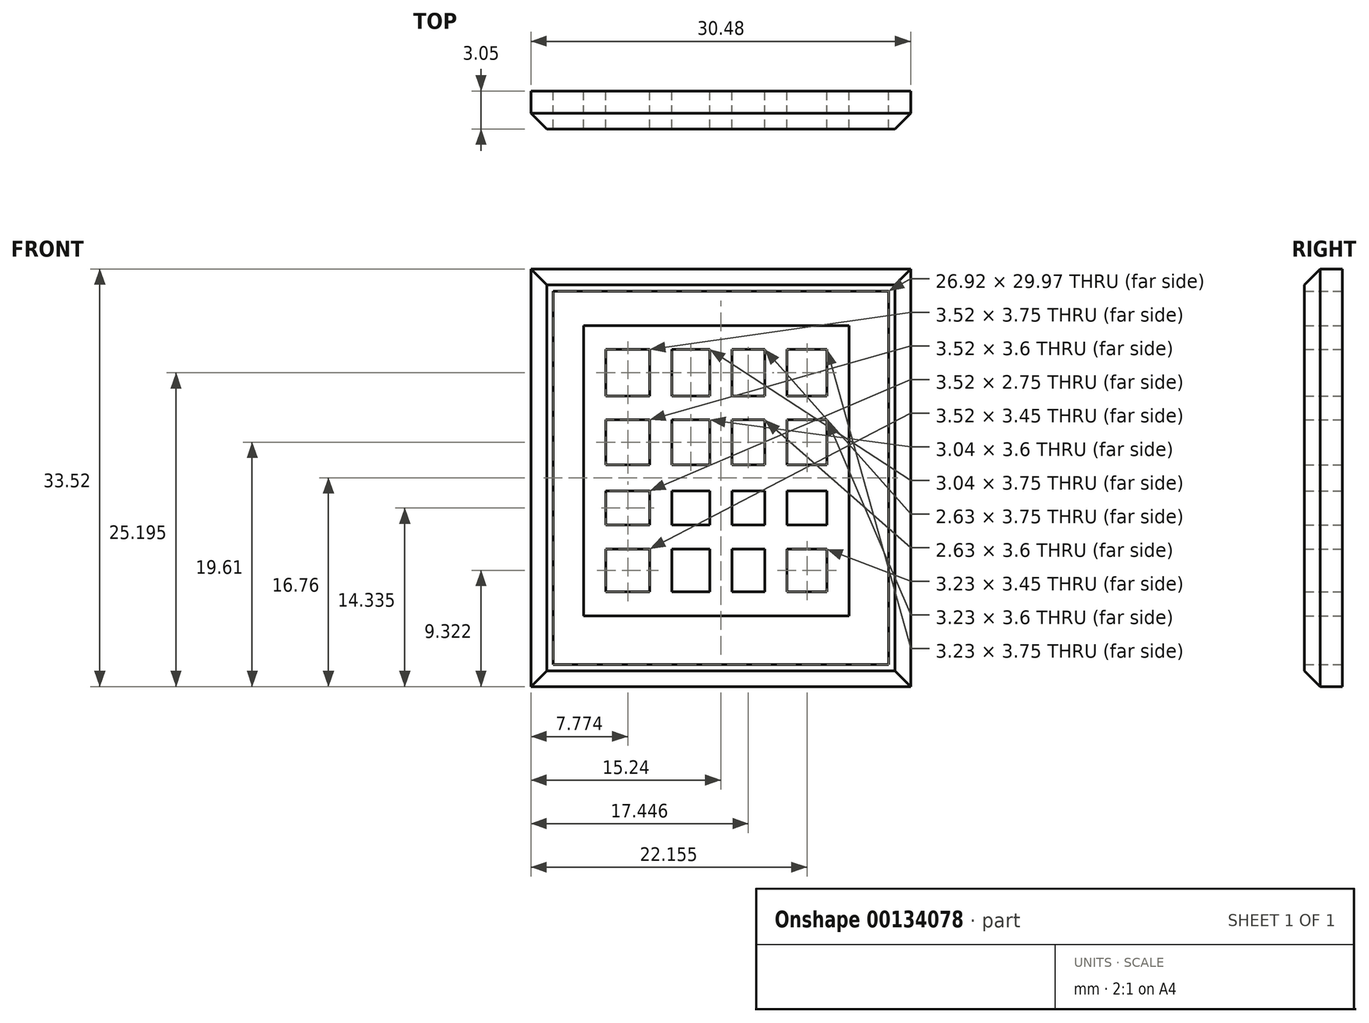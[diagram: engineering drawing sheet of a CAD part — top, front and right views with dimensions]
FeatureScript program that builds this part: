
annotation { "Feature Type Name" : "Feature", "Feature Type Description" : "" }
export const myFeature = defineFeature(function(context is Context, id is Id, definition is map)
    precondition{}
    {
        {
            var Q0;
            Q0=qCreatedBy(makeId("Front.planeOp"),FACE);
            var sketch = newSketch(context, id + "F0", { "sketchPlane" : qUnion([Q0])});
            skLineSegment(sketch, "E0.bottom", {"start": v(-15.24, 16.76) * mm, "end": v(15.24, 16.76) * mm});
            skLineSegment(sketch, "E0.top", {"start": v(-15.24, -16.76) * mm, "end": v(15.24, -16.76) * mm});
            skLineSegment(sketch, "E0.left", {"start": v(-15.24, 16.76) * mm, "end": v(-15.24, -16.76) * mm});
            skLineSegment(sketch, "E0.right", {"start": v(15.24, 16.76) * mm, "end": v(15.24, -16.76) * mm});
            skPoint(sketch, "E0.middle", {"position": v(0, 0) * mm});
            skLineSegment(sketch, "E1.bottom", {"start": v(-13.46, 14.99) * mm, "end": v(13.46, 14.99) * mm});
            skLineSegment(sketch, "E1.top", {"start": v(-13.46, -14.99) * mm, "end": v(13.46, -14.99) * mm});
            skLineSegment(sketch, "E1.left", {"start": v(-13.46, 14.99) * mm, "end": v(-13.46, -14.99) * mm});
            skLineSegment(sketch, "E1.right", {"start": v(13.46, 14.99) * mm, "end": v(13.46, -14.99) * mm});
            skLineSegment(sketch, "E2.bottom", {"start": v(-0.89, 14.99) * mm, "end": v(0.89, 14.99) * mm});
            skLineSegment(sketch, "E2.top", {"start": v(-0.89, -14.99) * mm, "end": v(0.89, -14.99) * mm});
            skLineSegment(sketch, "E2.left", {"start": v(-0.89, 14.99) * mm, "end": v(-0.89, -14.99) * mm});
            skLineSegment(sketch, "E2.right", {"start": v(0.89, 14.99) * mm, "end": v(0.89, -14.99) * mm});
            skLineSegment(sketch, "E3.bottom", {"start": v(3.52, 14.99) * mm, "end": v(5.3, 14.99) * mm});
            skLineSegment(sketch, "E3.top", {"start": v(3.52, -14.99) * mm, "end": v(5.3, -14.99) * mm});
            skLineSegment(sketch, "E3.left", {"start": v(3.52, 14.99) * mm, "end": v(3.52, -14.99) * mm});
            skLineSegment(sketch, "E3.right", {"start": v(5.3, 14.99) * mm, "end": v(5.3, -14.99) * mm});
            skPoint(sketch, "E3.middle", {"position": v(4.41, 0) * mm});
            skLineSegment(sketch, "E4.bottom", {"start": v(8.53, 14.99) * mm, "end": v(10.3, 14.99) * mm});
            skLineSegment(sketch, "E4.top", {"start": v(8.53, -14.99) * mm, "end": v(10.3, -14.99) * mm});
            skLineSegment(sketch, "E4.left", {"start": v(8.53, 14.99) * mm, "end": v(8.53, -14.99) * mm});
            skLineSegment(sketch, "E4.right", {"start": v(10.3, 14.99) * mm, "end": v(10.3, -14.99) * mm});
            skPoint(sketch, "E4.middle", {"position": v(9.42, 0) * mm});
            skLineSegment(sketch, "E5.bottom", {"start": v(-5.7, 14.99) * mm, "end": v(-3.93, 14.99) * mm});
            skLineSegment(sketch, "E5.top", {"start": v(-5.7, -14.99) * mm, "end": v(-3.93, -14.99) * mm});
            skLineSegment(sketch, "E5.left", {"start": v(-5.7, 14.99) * mm, "end": v(-5.7, -14.99) * mm});
            skLineSegment(sketch, "E5.right", {"start": v(-3.93, 14.99) * mm, "end": v(-3.93, -14.99) * mm});
            skPoint(sketch, "E5.middle", {"position": v(-4.82, 0) * mm});
            skLineSegment(sketch, "E6.bottom", {"start": v(-11, 14.99) * mm, "end": v(-9.23, 14.99) * mm});
            skLineSegment(sketch, "E6.top", {"start": v(-11, -14.99) * mm, "end": v(-9.23, -14.99) * mm});
            skLineSegment(sketch, "E6.left", {"start": v(-11, 14.99) * mm, "end": v(-11, -14.99) * mm});
            skLineSegment(sketch, "E6.right", {"start": v(-9.23, 14.99) * mm, "end": v(-9.23, -14.99) * mm});
            skPoint(sketch, "E6.middle", {"position": v(-10.12, 0) * mm});
            skLineSegment(sketch, "E7.bottom", {"start": v(-13.46, 1.05) * mm, "end": v(13.46, 1.05) * mm});
            skLineSegment(sketch, "E7.top", {"start": v(-13.46, -1.05) * mm, "end": v(13.46, -1.05) * mm});
            skLineSegment(sketch, "E7.left", {"start": v(-13.46, 1.05) * mm, "end": v(-13.46, -1.05) * mm});
            skLineSegment(sketch, "E7.right", {"start": v(13.46, 1.05) * mm, "end": v(13.46, -1.05) * mm});
            skLineSegment(sketch, "E8.bottom", {"start": v(-13.46, 6.56) * mm, "end": v(13.46, 6.56) * mm});
            skLineSegment(sketch, "E8.top", {"start": v(-13.46, 4.65) * mm, "end": v(13.46, 4.65) * mm});
            skLineSegment(sketch, "E8.left", {"start": v(-13.46, 6.56) * mm, "end": v(-13.46, 4.65) * mm});
            skLineSegment(sketch, "E8.right", {"start": v(13.46, 6.56) * mm, "end": v(13.46, 4.65) * mm});
            skPoint(sketch, "E8.middle", {"position": v(0, 5.6) * mm});
            skLineSegment(sketch, "E9.bottom", {"start": v(-13.46, 10.3) * mm, "end": v(13.46, 10.3) * mm});
            skLineSegment(sketch, "E9.top", {"start": v(-13.46, 12.22) * mm, "end": v(13.46, 12.22) * mm});
            skLineSegment(sketch, "E9.left", {"start": v(-13.46, 10.3) * mm, "end": v(-13.46, 12.22) * mm});
            skLineSegment(sketch, "E9.right", {"start": v(13.46, 10.3) * mm, "end": v(13.46, 12.22) * mm});
            skPoint(sketch, "E9.middle", {"position": v(0, 11.26) * mm});
            skLineSegment(sketch, "E10.bottom", {"start": v(-13.46, -5.71) * mm, "end": v(13.46, -5.71) * mm});
            skLineSegment(sketch, "E10.top", {"start": v(-13.46, -3.8) * mm, "end": v(13.46, -3.8) * mm});
            skLineSegment(sketch, "E10.left", {"start": v(-13.46, -5.71) * mm, "end": v(-13.46, -3.8) * mm});
            skLineSegment(sketch, "E10.right", {"start": v(13.46, -5.71) * mm, "end": v(13.46, -3.8) * mm});
            skPoint(sketch, "E10.middle", {"position": v(0, -4.76) * mm});
            skLineSegment(sketch, "E11.bottom", {"start": v(-13.46, -11.08) * mm, "end": v(13.46, -11.08) * mm});
            skLineSegment(sketch, "E11.top", {"start": v(-13.46, -9.16) * mm, "end": v(13.46, -9.16) * mm});
            skLineSegment(sketch, "E11.left", {"start": v(-13.46, -11.08) * mm, "end": v(-13.46, -9.16) * mm});
            skLineSegment(sketch, "E11.right", {"start": v(13.46, -11.08) * mm, "end": v(13.46, -9.16) * mm});
            skPoint(sketch, "E11.middle", {"position": v(0, -10.12) * mm});
            skSolve(sketch);
        }
        {
            var Q0;
            Q0=makeQuery(id+"F0.imprint","IMPRINT",FACE,{"disambiguationData":[TD([[makeQuery(id+"F0.imprint","IMPRINT",EDGE,{"derivedFrom":sQuery(id+"F0.wireOp",EDGE,"E0.bottom")}),-1.0]])]});
            var Q1;
            {var subQ0=sQuery(id+"F0.wireOp",EDGE,"E6.bottom");Q1=makeQuery(id+"F0.imprint","IMPRINT",FACE,{"disambiguationData":[TD([[makeQuery(id+"F0.imprint","IMPRINT",EDGE,{"derivedFrom":subQ0}),-1.0]])]});}
            var Q2;
            {var subQ0=sQuery(id+"F0.wireOp",EDGE,"E9.top");var subQ1=sQuery(id+"F0.wireOp",EDGE,"E6.left");var subQ2=makeQuery(id+"F0.imprint","INTERSECT",VERTEX,{"derivedFrom":[subQ1,subQ0]});Q2=makeQuery(id+"F0.imprint","IMPRINT",FACE,{"disambiguationData":[TD([[makeQuery(id+"F0.imprint","IMPRINT",EDGE,{"disambiguationData":[TD([[subQ2,-1.0]])],"derivedFrom":subQ1}),1.0]])]});}
            var Q3;
            {var subQ0=sQuery(id+"F0.wireOp",EDGE,"E9.bottom");var subQ1=sQuery(id+"F0.wireOp",EDGE,"E6.left");var subQ2=makeQuery(id+"F0.imprint","INTERSECT",VERTEX,{"derivedFrom":[subQ1,subQ0]});Q3=makeQuery(id+"F0.imprint","IMPRINT",FACE,{"disambiguationData":[TD([[makeQuery(id+"F0.imprint","IMPRINT",EDGE,{"disambiguationData":[TD([[subQ2,-1.0]])],"derivedFrom":subQ1}),1.0]])]});}
            var Q4;
            {var subQ0=sQuery(id+"F0.wireOp",EDGE,"E8.bottom");var subQ1=sQuery(id+"F0.wireOp",EDGE,"E6.left");var subQ2=makeQuery(id+"F0.imprint","INTERSECT",VERTEX,{"derivedFrom":[subQ1,subQ0]});Q4=makeQuery(id+"F0.imprint","IMPRINT",FACE,{"disambiguationData":[TD([[makeQuery(id+"F0.imprint","IMPRINT",EDGE,{"disambiguationData":[TD([[subQ2,-1.0]])],"derivedFrom":subQ1}),1.0]])]});}
            var Q5;
            {var subQ0=sQuery(id+"F0.wireOp",EDGE,"E8.top");var subQ1=sQuery(id+"F0.wireOp",EDGE,"E6.left");var subQ2=makeQuery(id+"F0.imprint","INTERSECT",VERTEX,{"derivedFrom":[subQ1,subQ0]});Q5=makeQuery(id+"F0.imprint","IMPRINT",FACE,{"disambiguationData":[TD([[makeQuery(id+"F0.imprint","IMPRINT",EDGE,{"disambiguationData":[TD([[subQ2,-1.0]])],"derivedFrom":subQ1}),1.0]])]});}
            var Q6;
            {var subQ0=sQuery(id+"F0.wireOp",EDGE,"E7.bottom");var subQ1=sQuery(id+"F0.wireOp",EDGE,"E6.left");var subQ2=makeQuery(id+"F0.imprint","INTERSECT",VERTEX,{"derivedFrom":[subQ1,subQ0]});Q6=makeQuery(id+"F0.imprint","IMPRINT",FACE,{"disambiguationData":[TD([[makeQuery(id+"F0.imprint","IMPRINT",EDGE,{"disambiguationData":[TD([[subQ2,-1.0]])],"derivedFrom":subQ1}),1.0]])]});}
            var Q7;
            {var subQ0=sQuery(id+"F0.wireOp",EDGE,"E7.top");var subQ1=sQuery(id+"F0.wireOp",EDGE,"E6.left");var subQ2=makeQuery(id+"F0.imprint","INTERSECT",VERTEX,{"derivedFrom":[subQ1,subQ0]});Q7=makeQuery(id+"F0.imprint","IMPRINT",FACE,{"disambiguationData":[TD([[makeQuery(id+"F0.imprint","IMPRINT",EDGE,{"disambiguationData":[TD([[subQ2,-1.0]])],"derivedFrom":subQ1}),1.0]])]});}
            var Q8;
            {var subQ0=sQuery(id+"F0.wireOp",EDGE,"E10.top");var subQ1=sQuery(id+"F0.wireOp",EDGE,"E6.left");var subQ2=makeQuery(id+"F0.imprint","INTERSECT",VERTEX,{"derivedFrom":[subQ1,subQ0]});Q8=makeQuery(id+"F0.imprint","IMPRINT",FACE,{"disambiguationData":[TD([[makeQuery(id+"F0.imprint","IMPRINT",EDGE,{"disambiguationData":[TD([[subQ2,-1.0]])],"derivedFrom":subQ1}),1.0]])]});}
            var Q9;
            {var subQ0=sQuery(id+"F0.wireOp",EDGE,"E10.bottom");var subQ1=sQuery(id+"F0.wireOp",EDGE,"E6.left");var subQ2=makeQuery(id+"F0.imprint","INTERSECT",VERTEX,{"derivedFrom":[subQ1,subQ0]});Q9=makeQuery(id+"F0.imprint","IMPRINT",FACE,{"disambiguationData":[TD([[makeQuery(id+"F0.imprint","IMPRINT",EDGE,{"disambiguationData":[TD([[subQ2,-1.0]])],"derivedFrom":subQ1}),1.0]])]});}
            var Q10;
            {var subQ0=sQuery(id+"F0.wireOp",EDGE,"E11.top");var subQ1=sQuery(id+"F0.wireOp",EDGE,"E6.left");var subQ2=makeQuery(id+"F0.imprint","INTERSECT",VERTEX,{"derivedFrom":[subQ1,subQ0]});Q10=makeQuery(id+"F0.imprint","IMPRINT",FACE,{"disambiguationData":[TD([[makeQuery(id+"F0.imprint","IMPRINT",EDGE,{"disambiguationData":[TD([[subQ2,-1.0]])],"derivedFrom":subQ1}),1.0]])]});}
            var Q11;
            {var subQ0=sQuery(id+"F0.wireOp",EDGE,"E6.top");Q11=makeQuery(id+"F0.imprint","IMPRINT",FACE,{"disambiguationData":[TD([[makeQuery(id+"F0.imprint","IMPRINT",EDGE,{"derivedFrom":subQ0}),1.0]])]});}
            var Q12;
            {var subQ0=sQuery(id+"F0.wireOp",EDGE,"E5.top");Q12=makeQuery(id+"F0.imprint","IMPRINT",FACE,{"disambiguationData":[TD([[makeQuery(id+"F0.imprint","IMPRINT",EDGE,{"derivedFrom":subQ0}),1.0]])]});}
            var Q13;
            {var subQ0=sQuery(id+"F0.wireOp",EDGE,"E11.top");var subQ1=sQuery(id+"F0.wireOp",EDGE,"E5.left");var subQ2=makeQuery(id+"F0.imprint","INTERSECT",VERTEX,{"derivedFrom":[subQ1,subQ0]});Q13=makeQuery(id+"F0.imprint","IMPRINT",FACE,{"disambiguationData":[TD([[makeQuery(id+"F0.imprint","IMPRINT",EDGE,{"disambiguationData":[TD([[subQ2,-1.0]])],"derivedFrom":subQ1}),1.0]])]});}
            var Q14;
            {var subQ0=sQuery(id+"F0.wireOp",EDGE,"E10.bottom");var subQ1=sQuery(id+"F0.wireOp",EDGE,"E5.left");var subQ2=makeQuery(id+"F0.imprint","INTERSECT",VERTEX,{"derivedFrom":[subQ1,subQ0]});Q14=makeQuery(id+"F0.imprint","IMPRINT",FACE,{"disambiguationData":[TD([[makeQuery(id+"F0.imprint","IMPRINT",EDGE,{"disambiguationData":[TD([[subQ2,-1.0]])],"derivedFrom":subQ1}),1.0]])]});}
            var Q15;
            {var subQ0=sQuery(id+"F0.wireOp",EDGE,"E10.top");var subQ1=sQuery(id+"F0.wireOp",EDGE,"E5.left");var subQ2=makeQuery(id+"F0.imprint","INTERSECT",VERTEX,{"derivedFrom":[subQ1,subQ0]});Q15=makeQuery(id+"F0.imprint","IMPRINT",FACE,{"disambiguationData":[TD([[makeQuery(id+"F0.imprint","IMPRINT",EDGE,{"disambiguationData":[TD([[subQ2,-1.0]])],"derivedFrom":subQ1}),1.0]])]});}
            var Q16;
            {var subQ0=sQuery(id+"F0.wireOp",EDGE,"E7.top");var subQ1=sQuery(id+"F0.wireOp",EDGE,"E5.left");var subQ2=makeQuery(id+"F0.imprint","INTERSECT",VERTEX,{"derivedFrom":[subQ1,subQ0]});Q16=makeQuery(id+"F0.imprint","IMPRINT",FACE,{"disambiguationData":[TD([[makeQuery(id+"F0.imprint","IMPRINT",EDGE,{"disambiguationData":[TD([[subQ2,-1.0]])],"derivedFrom":subQ1}),1.0]])]});}
            var Q17;
            {var subQ0=sQuery(id+"F0.wireOp",EDGE,"E7.bottom");var subQ1=sQuery(id+"F0.wireOp",EDGE,"E5.left");var subQ2=makeQuery(id+"F0.imprint","INTERSECT",VERTEX,{"derivedFrom":[subQ1,subQ0]});Q17=makeQuery(id+"F0.imprint","IMPRINT",FACE,{"disambiguationData":[TD([[makeQuery(id+"F0.imprint","IMPRINT",EDGE,{"disambiguationData":[TD([[subQ2,-1.0]])],"derivedFrom":subQ1}),1.0]])]});}
            var Q18;
            {var subQ0=sQuery(id+"F0.wireOp",EDGE,"E8.top");var subQ1=sQuery(id+"F0.wireOp",EDGE,"E5.left");var subQ2=makeQuery(id+"F0.imprint","INTERSECT",VERTEX,{"derivedFrom":[subQ1,subQ0]});Q18=makeQuery(id+"F0.imprint","IMPRINT",FACE,{"disambiguationData":[TD([[makeQuery(id+"F0.imprint","IMPRINT",EDGE,{"disambiguationData":[TD([[subQ2,-1.0]])],"derivedFrom":subQ1}),1.0]])]});}
            var Q19;
            {var subQ0=sQuery(id+"F0.wireOp",EDGE,"E8.bottom");var subQ1=sQuery(id+"F0.wireOp",EDGE,"E5.left");var subQ2=makeQuery(id+"F0.imprint","INTERSECT",VERTEX,{"derivedFrom":[subQ1,subQ0]});Q19=makeQuery(id+"F0.imprint","IMPRINT",FACE,{"disambiguationData":[TD([[makeQuery(id+"F0.imprint","IMPRINT",EDGE,{"disambiguationData":[TD([[subQ2,-1.0]])],"derivedFrom":subQ1}),1.0]])]});}
            var Q20;
            {var subQ0=sQuery(id+"F0.wireOp",EDGE,"E9.bottom");var subQ1=sQuery(id+"F0.wireOp",EDGE,"E5.left");var subQ2=makeQuery(id+"F0.imprint","INTERSECT",VERTEX,{"derivedFrom":[subQ1,subQ0]});Q20=makeQuery(id+"F0.imprint","IMPRINT",FACE,{"disambiguationData":[TD([[makeQuery(id+"F0.imprint","IMPRINT",EDGE,{"disambiguationData":[TD([[subQ2,-1.0]])],"derivedFrom":subQ1}),1.0]])]});}
            var Q21;
            {var subQ0=sQuery(id+"F0.wireOp",EDGE,"E9.top");var subQ1=sQuery(id+"F0.wireOp",EDGE,"E5.left");var subQ2=makeQuery(id+"F0.imprint","INTERSECT",VERTEX,{"derivedFrom":[subQ1,subQ0]});Q21=makeQuery(id+"F0.imprint","IMPRINT",FACE,{"disambiguationData":[TD([[makeQuery(id+"F0.imprint","IMPRINT",EDGE,{"disambiguationData":[TD([[subQ2,-1.0]])],"derivedFrom":subQ1}),1.0]])]});}
            var Q22;
            {var subQ0=sQuery(id+"F0.wireOp",EDGE,"E5.bottom");Q22=makeQuery(id+"F0.imprint","IMPRINT",FACE,{"disambiguationData":[TD([[makeQuery(id+"F0.imprint","IMPRINT",EDGE,{"derivedFrom":subQ0}),-1.0]])]});}
            var Q23;
            {var subQ0=sQuery(id+"F0.wireOp",EDGE,"E2.bottom");Q23=makeQuery(id+"F0.imprint","IMPRINT",FACE,{"disambiguationData":[TD([[makeQuery(id+"F0.imprint","IMPRINT",EDGE,{"derivedFrom":subQ0}),-1.0]])]});}
            var Q24;
            {var subQ0=sQuery(id+"F0.wireOp",EDGE,"E9.top");var subQ1=sQuery(id+"F0.wireOp",EDGE,"E2.left");var subQ2=makeQuery(id+"F0.imprint","INTERSECT",VERTEX,{"derivedFrom":[subQ1,subQ0]});Q24=makeQuery(id+"F0.imprint","IMPRINT",FACE,{"disambiguationData":[TD([[makeQuery(id+"F0.imprint","IMPRINT",EDGE,{"disambiguationData":[TD([[subQ2,-1.0]])],"derivedFrom":subQ1}),1.0]])]});}
            var Q25;
            {var subQ0=sQuery(id+"F0.wireOp",EDGE,"E9.bottom");var subQ1=sQuery(id+"F0.wireOp",EDGE,"E2.left");var subQ2=makeQuery(id+"F0.imprint","INTERSECT",VERTEX,{"derivedFrom":[subQ1,subQ0]});Q25=makeQuery(id+"F0.imprint","IMPRINT",FACE,{"disambiguationData":[TD([[makeQuery(id+"F0.imprint","IMPRINT",EDGE,{"disambiguationData":[TD([[subQ2,-1.0]])],"derivedFrom":subQ1}),1.0]])]});}
            var Q26;
            {var subQ0=sQuery(id+"F0.wireOp",EDGE,"E8.bottom");var subQ1=sQuery(id+"F0.wireOp",EDGE,"E2.left");var subQ2=makeQuery(id+"F0.imprint","INTERSECT",VERTEX,{"derivedFrom":[subQ1,subQ0]});Q26=makeQuery(id+"F0.imprint","IMPRINT",FACE,{"disambiguationData":[TD([[makeQuery(id+"F0.imprint","IMPRINT",EDGE,{"disambiguationData":[TD([[subQ2,-1.0]])],"derivedFrom":subQ1}),1.0]])]});}
            var Q27;
            {var subQ0=sQuery(id+"F0.wireOp",EDGE,"E8.top");var subQ1=sQuery(id+"F0.wireOp",EDGE,"E2.left");var subQ2=makeQuery(id+"F0.imprint","INTERSECT",VERTEX,{"derivedFrom":[subQ1,subQ0]});Q27=makeQuery(id+"F0.imprint","IMPRINT",FACE,{"disambiguationData":[TD([[makeQuery(id+"F0.imprint","IMPRINT",EDGE,{"disambiguationData":[TD([[subQ2,-1.0]])],"derivedFrom":subQ1}),1.0]])]});}
            var Q28;
            {var subQ0=sQuery(id+"F0.wireOp",EDGE,"E7.bottom");var subQ1=sQuery(id+"F0.wireOp",EDGE,"E2.left");var subQ2=makeQuery(id+"F0.imprint","INTERSECT",VERTEX,{"derivedFrom":[subQ1,subQ0]});Q28=makeQuery(id+"F0.imprint","IMPRINT",FACE,{"disambiguationData":[TD([[makeQuery(id+"F0.imprint","IMPRINT",EDGE,{"disambiguationData":[TD([[subQ2,-1.0]])],"derivedFrom":subQ1}),1.0]])]});}
            var Q29;
            {var subQ0=sQuery(id+"F0.wireOp",EDGE,"E7.top");var subQ1=sQuery(id+"F0.wireOp",EDGE,"E2.left");var subQ2=makeQuery(id+"F0.imprint","INTERSECT",VERTEX,{"derivedFrom":[subQ1,subQ0]});Q29=makeQuery(id+"F0.imprint","IMPRINT",FACE,{"disambiguationData":[TD([[makeQuery(id+"F0.imprint","IMPRINT",EDGE,{"disambiguationData":[TD([[subQ2,-1.0]])],"derivedFrom":subQ1}),1.0]])]});}
            var Q30;
            {var subQ0=sQuery(id+"F0.wireOp",EDGE,"E10.top");var subQ1=sQuery(id+"F0.wireOp",EDGE,"E2.left");var subQ2=makeQuery(id+"F0.imprint","INTERSECT",VERTEX,{"derivedFrom":[subQ1,subQ0]});Q30=makeQuery(id+"F0.imprint","IMPRINT",FACE,{"disambiguationData":[TD([[makeQuery(id+"F0.imprint","IMPRINT",EDGE,{"disambiguationData":[TD([[subQ2,-1.0]])],"derivedFrom":subQ1}),1.0]])]});}
            var Q31;
            {var subQ0=sQuery(id+"F0.wireOp",EDGE,"E10.bottom");var subQ1=sQuery(id+"F0.wireOp",EDGE,"E2.left");var subQ2=makeQuery(id+"F0.imprint","INTERSECT",VERTEX,{"derivedFrom":[subQ1,subQ0]});Q31=makeQuery(id+"F0.imprint","IMPRINT",FACE,{"disambiguationData":[TD([[makeQuery(id+"F0.imprint","IMPRINT",EDGE,{"disambiguationData":[TD([[subQ2,-1.0]])],"derivedFrom":subQ1}),1.0]])]});}
            var Q32;
            {var subQ0=sQuery(id+"F0.wireOp",EDGE,"E11.top");var subQ1=sQuery(id+"F0.wireOp",EDGE,"E2.left");var subQ2=makeQuery(id+"F0.imprint","INTERSECT",VERTEX,{"derivedFrom":[subQ1,subQ0]});Q32=makeQuery(id+"F0.imprint","IMPRINT",FACE,{"disambiguationData":[TD([[makeQuery(id+"F0.imprint","IMPRINT",EDGE,{"disambiguationData":[TD([[subQ2,-1.0]])],"derivedFrom":subQ1}),1.0]])]});}
            var Q33;
            {var subQ0=sQuery(id+"F0.wireOp",EDGE,"E2.top");Q33=makeQuery(id+"F0.imprint","IMPRINT",FACE,{"disambiguationData":[TD([[makeQuery(id+"F0.imprint","IMPRINT",EDGE,{"derivedFrom":subQ0}),1.0]])]});}
            var Q34;
            {var subQ0=sQuery(id+"F0.wireOp",EDGE,"E3.top");Q34=makeQuery(id+"F0.imprint","IMPRINT",FACE,{"disambiguationData":[TD([[makeQuery(id+"F0.imprint","IMPRINT",EDGE,{"derivedFrom":subQ0}),1.0]])]});}
            var Q35;
            {var subQ0=sQuery(id+"F0.wireOp",EDGE,"E11.top");var subQ1=sQuery(id+"F0.wireOp",EDGE,"E3.left");var subQ2=makeQuery(id+"F0.imprint","INTERSECT",VERTEX,{"derivedFrom":[subQ1,subQ0]});Q35=makeQuery(id+"F0.imprint","IMPRINT",FACE,{"disambiguationData":[TD([[makeQuery(id+"F0.imprint","IMPRINT",EDGE,{"disambiguationData":[TD([[subQ2,-1.0]])],"derivedFrom":subQ1}),1.0]])]});}
            var Q36;
            {var subQ0=sQuery(id+"F0.wireOp",EDGE,"E10.bottom");var subQ1=sQuery(id+"F0.wireOp",EDGE,"E3.left");var subQ2=makeQuery(id+"F0.imprint","INTERSECT",VERTEX,{"derivedFrom":[subQ1,subQ0]});Q36=makeQuery(id+"F0.imprint","IMPRINT",FACE,{"disambiguationData":[TD([[makeQuery(id+"F0.imprint","IMPRINT",EDGE,{"disambiguationData":[TD([[subQ2,-1.0]])],"derivedFrom":subQ1}),1.0]])]});}
            var Q37;
            {var subQ0=sQuery(id+"F0.wireOp",EDGE,"E10.top");var subQ1=sQuery(id+"F0.wireOp",EDGE,"E3.left");var subQ2=makeQuery(id+"F0.imprint","INTERSECT",VERTEX,{"derivedFrom":[subQ1,subQ0]});Q37=makeQuery(id+"F0.imprint","IMPRINT",FACE,{"disambiguationData":[TD([[makeQuery(id+"F0.imprint","IMPRINT",EDGE,{"disambiguationData":[TD([[subQ2,-1.0]])],"derivedFrom":subQ1}),1.0]])]});}
            var Q38;
            {var subQ0=sQuery(id+"F0.wireOp",EDGE,"E7.top");var subQ1=sQuery(id+"F0.wireOp",EDGE,"E3.left");var subQ2=makeQuery(id+"F0.imprint","INTERSECT",VERTEX,{"derivedFrom":[subQ1,subQ0]});Q38=makeQuery(id+"F0.imprint","IMPRINT",FACE,{"disambiguationData":[TD([[makeQuery(id+"F0.imprint","IMPRINT",EDGE,{"disambiguationData":[TD([[subQ2,-1.0]])],"derivedFrom":subQ1}),1.0]])]});}
            var Q39;
            {var subQ0=sQuery(id+"F0.wireOp",EDGE,"E7.bottom");var subQ1=sQuery(id+"F0.wireOp",EDGE,"E3.left");var subQ2=makeQuery(id+"F0.imprint","INTERSECT",VERTEX,{"derivedFrom":[subQ1,subQ0]});Q39=makeQuery(id+"F0.imprint","IMPRINT",FACE,{"disambiguationData":[TD([[makeQuery(id+"F0.imprint","IMPRINT",EDGE,{"disambiguationData":[TD([[subQ2,-1.0]])],"derivedFrom":subQ1}),1.0]])]});}
            var Q40;
            {var subQ0=sQuery(id+"F0.wireOp",EDGE,"E8.top");var subQ1=sQuery(id+"F0.wireOp",EDGE,"E3.left");var subQ2=makeQuery(id+"F0.imprint","INTERSECT",VERTEX,{"derivedFrom":[subQ1,subQ0]});Q40=makeQuery(id+"F0.imprint","IMPRINT",FACE,{"disambiguationData":[TD([[makeQuery(id+"F0.imprint","IMPRINT",EDGE,{"disambiguationData":[TD([[subQ2,-1.0]])],"derivedFrom":subQ1}),1.0]])]});}
            var Q41;
            {var subQ0=sQuery(id+"F0.wireOp",EDGE,"E8.bottom");var subQ1=sQuery(id+"F0.wireOp",EDGE,"E3.left");var subQ2=makeQuery(id+"F0.imprint","INTERSECT",VERTEX,{"derivedFrom":[subQ1,subQ0]});Q41=makeQuery(id+"F0.imprint","IMPRINT",FACE,{"disambiguationData":[TD([[makeQuery(id+"F0.imprint","IMPRINT",EDGE,{"disambiguationData":[TD([[subQ2,-1.0]])],"derivedFrom":subQ1}),1.0]])]});}
            var Q42;
            {var subQ0=sQuery(id+"F0.wireOp",EDGE,"E9.bottom");var subQ1=sQuery(id+"F0.wireOp",EDGE,"E3.left");var subQ2=makeQuery(id+"F0.imprint","INTERSECT",VERTEX,{"derivedFrom":[subQ1,subQ0]});Q42=makeQuery(id+"F0.imprint","IMPRINT",FACE,{"disambiguationData":[TD([[makeQuery(id+"F0.imprint","IMPRINT",EDGE,{"disambiguationData":[TD([[subQ2,-1.0]])],"derivedFrom":subQ1}),1.0]])]});}
            var Q43;
            {var subQ0=sQuery(id+"F0.wireOp",EDGE,"E9.top");var subQ1=sQuery(id+"F0.wireOp",EDGE,"E3.left");var subQ2=makeQuery(id+"F0.imprint","INTERSECT",VERTEX,{"derivedFrom":[subQ1,subQ0]});Q43=makeQuery(id+"F0.imprint","IMPRINT",FACE,{"disambiguationData":[TD([[makeQuery(id+"F0.imprint","IMPRINT",EDGE,{"disambiguationData":[TD([[subQ2,-1.0]])],"derivedFrom":subQ1}),1.0]])]});}
            var Q44;
            {var subQ0=sQuery(id+"F0.wireOp",EDGE,"E3.bottom");Q44=makeQuery(id+"F0.imprint","IMPRINT",FACE,{"disambiguationData":[TD([[makeQuery(id+"F0.imprint","IMPRINT",EDGE,{"derivedFrom":subQ0}),-1.0]])]});}
            var Q45;
            {var subQ0=sQuery(id+"F0.wireOp",EDGE,"E4.bottom");Q45=makeQuery(id+"F0.imprint","IMPRINT",FACE,{"disambiguationData":[TD([[makeQuery(id+"F0.imprint","IMPRINT",EDGE,{"derivedFrom":subQ0}),-1.0]])]});}
            var Q46;
            {var subQ0=sQuery(id+"F0.wireOp",EDGE,"E9.top");var subQ1=sQuery(id+"F0.wireOp",EDGE,"E4.left");var subQ2=makeQuery(id+"F0.imprint","INTERSECT",VERTEX,{"derivedFrom":[subQ1,subQ0]});Q46=makeQuery(id+"F0.imprint","IMPRINT",FACE,{"disambiguationData":[TD([[makeQuery(id+"F0.imprint","IMPRINT",EDGE,{"disambiguationData":[TD([[subQ2,-1.0]])],"derivedFrom":subQ1}),1.0]])]});}
            var Q47;
            {var subQ0=sQuery(id+"F0.wireOp",EDGE,"E9.bottom");var subQ1=sQuery(id+"F0.wireOp",EDGE,"E4.left");var subQ2=makeQuery(id+"F0.imprint","INTERSECT",VERTEX,{"derivedFrom":[subQ1,subQ0]});Q47=makeQuery(id+"F0.imprint","IMPRINT",FACE,{"disambiguationData":[TD([[makeQuery(id+"F0.imprint","IMPRINT",EDGE,{"disambiguationData":[TD([[subQ2,-1.0]])],"derivedFrom":subQ1}),1.0]])]});}
            var Q48;
            {var subQ0=sQuery(id+"F0.wireOp",EDGE,"E8.bottom");var subQ1=sQuery(id+"F0.wireOp",EDGE,"E4.left");var subQ2=makeQuery(id+"F0.imprint","INTERSECT",VERTEX,{"derivedFrom":[subQ1,subQ0]});Q48=makeQuery(id+"F0.imprint","IMPRINT",FACE,{"disambiguationData":[TD([[makeQuery(id+"F0.imprint","IMPRINT",EDGE,{"disambiguationData":[TD([[subQ2,-1.0]])],"derivedFrom":subQ1}),1.0]])]});}
            var Q49;
            {var subQ0=sQuery(id+"F0.wireOp",EDGE,"E8.top");var subQ1=sQuery(id+"F0.wireOp",EDGE,"E4.left");var subQ2=makeQuery(id+"F0.imprint","INTERSECT",VERTEX,{"derivedFrom":[subQ1,subQ0]});Q49=makeQuery(id+"F0.imprint","IMPRINT",FACE,{"disambiguationData":[TD([[makeQuery(id+"F0.imprint","IMPRINT",EDGE,{"disambiguationData":[TD([[subQ2,-1.0]])],"derivedFrom":subQ1}),1.0]])]});}
            var Q50;
            {var subQ0=sQuery(id+"F0.wireOp",EDGE,"E7.bottom");var subQ1=sQuery(id+"F0.wireOp",EDGE,"E4.left");var subQ2=makeQuery(id+"F0.imprint","INTERSECT",VERTEX,{"derivedFrom":[subQ1,subQ0]});Q50=makeQuery(id+"F0.imprint","IMPRINT",FACE,{"disambiguationData":[TD([[makeQuery(id+"F0.imprint","IMPRINT",EDGE,{"disambiguationData":[TD([[subQ2,-1.0]])],"derivedFrom":subQ1}),1.0]])]});}
            var Q51;
            {var subQ0=sQuery(id+"F0.wireOp",EDGE,"E7.top");var subQ1=sQuery(id+"F0.wireOp",EDGE,"E4.left");var subQ2=makeQuery(id+"F0.imprint","INTERSECT",VERTEX,{"derivedFrom":[subQ1,subQ0]});Q51=makeQuery(id+"F0.imprint","IMPRINT",FACE,{"disambiguationData":[TD([[makeQuery(id+"F0.imprint","IMPRINT",EDGE,{"disambiguationData":[TD([[subQ2,-1.0]])],"derivedFrom":subQ1}),1.0]])]});}
            var Q52;
            {var subQ0=sQuery(id+"F0.wireOp",EDGE,"E10.top");var subQ1=sQuery(id+"F0.wireOp",EDGE,"E4.left");var subQ2=makeQuery(id+"F0.imprint","INTERSECT",VERTEX,{"derivedFrom":[subQ1,subQ0]});Q52=makeQuery(id+"F0.imprint","IMPRINT",FACE,{"disambiguationData":[TD([[makeQuery(id+"F0.imprint","IMPRINT",EDGE,{"disambiguationData":[TD([[subQ2,-1.0]])],"derivedFrom":subQ1}),1.0]])]});}
            var Q53;
            {var subQ0=sQuery(id+"F0.wireOp",EDGE,"E10.bottom");var subQ1=sQuery(id+"F0.wireOp",EDGE,"E4.left");var subQ2=makeQuery(id+"F0.imprint","INTERSECT",VERTEX,{"derivedFrom":[subQ1,subQ0]});Q53=makeQuery(id+"F0.imprint","IMPRINT",FACE,{"disambiguationData":[TD([[makeQuery(id+"F0.imprint","IMPRINT",EDGE,{"disambiguationData":[TD([[subQ2,-1.0]])],"derivedFrom":subQ1}),1.0]])]});}
            var Q54;
            {var subQ0=sQuery(id+"F0.wireOp",EDGE,"E11.top");var subQ1=sQuery(id+"F0.wireOp",EDGE,"E4.left");var subQ2=makeQuery(id+"F0.imprint","INTERSECT",VERTEX,{"derivedFrom":[subQ1,subQ0]});Q54=makeQuery(id+"F0.imprint","IMPRINT",FACE,{"disambiguationData":[TD([[makeQuery(id+"F0.imprint","IMPRINT",EDGE,{"disambiguationData":[TD([[subQ2,-1.0]])],"derivedFrom":subQ1}),1.0]])]});}
            var Q55;
            {var subQ0=sQuery(id+"F0.wireOp",EDGE,"E4.top");Q55=makeQuery(id+"F0.imprint","IMPRINT",FACE,{"disambiguationData":[TD([[makeQuery(id+"F0.imprint","IMPRINT",EDGE,{"derivedFrom":subQ0}),1.0]])]});}
            var Q56;
            {var subQ5=sQuery(id+"F0.wireOp",EDGE,"E11.right");Q56=makeQuery(id+"F0.imprint","IMPRINT",FACE,{"disambiguationData":[TD([[makeQuery(id+"F0.imprint","IMPRINT",EDGE,{"derivedFrom":subQ5}),1.0]])]});}
            var Q57;
            {var subQ0=sQuery(id+"F0.wireOp",EDGE,"E11.top");var subQ1=sQuery(id+"F0.wireOp",EDGE,"E3.right");var subQ2=makeQuery(id+"F0.imprint","INTERSECT",VERTEX,{"derivedFrom":[subQ1,subQ0]});Q57=makeQuery(id+"F0.imprint","IMPRINT",FACE,{"disambiguationData":[TD([[makeQuery(id+"F0.imprint","IMPRINT",EDGE,{"disambiguationData":[TD([[subQ2,-1.0]])],"derivedFrom":subQ1}),1.0]])]});}
            var Q58;
            {var subQ0=sQuery(id+"F0.wireOp",EDGE,"E11.top");var subQ1=sQuery(id+"F0.wireOp",EDGE,"E2.right");var subQ2=makeQuery(id+"F0.imprint","INTERSECT",VERTEX,{"derivedFrom":[subQ1,subQ0]});Q58=makeQuery(id+"F0.imprint","IMPRINT",FACE,{"disambiguationData":[TD([[makeQuery(id+"F0.imprint","IMPRINT",EDGE,{"disambiguationData":[TD([[subQ2,-1.0]])],"derivedFrom":subQ1}),1.0]])]});}
            var Q59;
            {var subQ0=sQuery(id+"F0.wireOp",EDGE,"E11.top");var subQ1=sQuery(id+"F0.wireOp",EDGE,"E2.left");var subQ2=makeQuery(id+"F0.imprint","INTERSECT",VERTEX,{"derivedFrom":[subQ1,subQ0]});Q59=makeQuery(id+"F0.imprint","IMPRINT",FACE,{"disambiguationData":[TD([[makeQuery(id+"F0.imprint","IMPRINT",EDGE,{"disambiguationData":[TD([[subQ2,-1.0]])],"derivedFrom":subQ1}),-1.0]])]});}
            var Q60;
            {var subQ0=sQuery(id+"F0.wireOp",EDGE,"E11.top");var subQ1=sQuery(id+"F0.wireOp",EDGE,"E5.left");var subQ2=makeQuery(id+"F0.imprint","INTERSECT",VERTEX,{"derivedFrom":[subQ1,subQ0]});Q60=makeQuery(id+"F0.imprint","IMPRINT",FACE,{"disambiguationData":[TD([[makeQuery(id+"F0.imprint","IMPRINT",EDGE,{"disambiguationData":[TD([[subQ2,-1.0]])],"derivedFrom":subQ1}),-1.0]])]});}
            var Q61;
            {var subQ5=sQuery(id+"F0.wireOp",EDGE,"E11.left");Q61=makeQuery(id+"F0.imprint","IMPRINT",FACE,{"disambiguationData":[TD([[makeQuery(id+"F0.imprint","IMPRINT",EDGE,{"derivedFrom":subQ5}),-1.0]])]});}
            var Q62;
            {var subQ5=sQuery(id+"F0.wireOp",EDGE,"E10.left");Q62=makeQuery(id+"F0.imprint","IMPRINT",FACE,{"disambiguationData":[TD([[makeQuery(id+"F0.imprint","IMPRINT",EDGE,{"derivedFrom":subQ5}),-1.0]])]});}
            var Q63;
            {var subQ0=sQuery(id+"F0.wireOp",EDGE,"E10.top");var subQ1=sQuery(id+"F0.wireOp",EDGE,"E5.left");var subQ2=makeQuery(id+"F0.imprint","INTERSECT",VERTEX,{"derivedFrom":[subQ1,subQ0]});Q63=makeQuery(id+"F0.imprint","IMPRINT",FACE,{"disambiguationData":[TD([[makeQuery(id+"F0.imprint","IMPRINT",EDGE,{"disambiguationData":[TD([[subQ2,-1.0]])],"derivedFrom":subQ1}),-1.0]])]});}
            var Q64;
            {var subQ0=sQuery(id+"F0.wireOp",EDGE,"E10.top");var subQ1=sQuery(id+"F0.wireOp",EDGE,"E2.left");var subQ2=makeQuery(id+"F0.imprint","INTERSECT",VERTEX,{"derivedFrom":[subQ1,subQ0]});Q64=makeQuery(id+"F0.imprint","IMPRINT",FACE,{"disambiguationData":[TD([[makeQuery(id+"F0.imprint","IMPRINT",EDGE,{"disambiguationData":[TD([[subQ2,-1.0]])],"derivedFrom":subQ1}),-1.0]])]});}
            var Q65;
            {var subQ0=sQuery(id+"F0.wireOp",EDGE,"E10.top");var subQ1=sQuery(id+"F0.wireOp",EDGE,"E2.right");var subQ2=makeQuery(id+"F0.imprint","INTERSECT",VERTEX,{"derivedFrom":[subQ1,subQ0]});Q65=makeQuery(id+"F0.imprint","IMPRINT",FACE,{"disambiguationData":[TD([[makeQuery(id+"F0.imprint","IMPRINT",EDGE,{"disambiguationData":[TD([[subQ2,-1.0]])],"derivedFrom":subQ1}),1.0]])]});}
            var Q66;
            {var subQ0=sQuery(id+"F0.wireOp",EDGE,"E10.top");var subQ1=sQuery(id+"F0.wireOp",EDGE,"E3.right");var subQ2=makeQuery(id+"F0.imprint","INTERSECT",VERTEX,{"derivedFrom":[subQ1,subQ0]});Q66=makeQuery(id+"F0.imprint","IMPRINT",FACE,{"disambiguationData":[TD([[makeQuery(id+"F0.imprint","IMPRINT",EDGE,{"disambiguationData":[TD([[subQ2,-1.0]])],"derivedFrom":subQ1}),1.0]])]});}
            var Q67;
            {var subQ5=sQuery(id+"F0.wireOp",EDGE,"E10.right");Q67=makeQuery(id+"F0.imprint","IMPRINT",FACE,{"disambiguationData":[TD([[makeQuery(id+"F0.imprint","IMPRINT",EDGE,{"derivedFrom":subQ5}),1.0]])]});}
            var Q68;
            {var subQ5=sQuery(id+"F0.wireOp",EDGE,"E7.right");Q68=makeQuery(id+"F0.imprint","IMPRINT",FACE,{"disambiguationData":[TD([[makeQuery(id+"F0.imprint","IMPRINT",EDGE,{"derivedFrom":subQ5}),-1.0]])]});}
            var Q69;
            {var subQ0=sQuery(id+"F0.wireOp",EDGE,"E7.bottom");var subQ1=sQuery(id+"F0.wireOp",EDGE,"E3.right");var subQ2=makeQuery(id+"F0.imprint","INTERSECT",VERTEX,{"derivedFrom":[subQ1,subQ0]});Q69=makeQuery(id+"F0.imprint","IMPRINT",FACE,{"disambiguationData":[TD([[makeQuery(id+"F0.imprint","IMPRINT",EDGE,{"disambiguationData":[TD([[subQ2,-1.0]])],"derivedFrom":subQ1}),1.0]])]});}
            var Q70;
            {var subQ0=sQuery(id+"F0.wireOp",EDGE,"E7.bottom");var subQ1=sQuery(id+"F0.wireOp",EDGE,"E2.right");var subQ2=makeQuery(id+"F0.imprint","INTERSECT",VERTEX,{"derivedFrom":[subQ1,subQ0]});Q70=makeQuery(id+"F0.imprint","IMPRINT",FACE,{"disambiguationData":[TD([[makeQuery(id+"F0.imprint","IMPRINT",EDGE,{"disambiguationData":[TD([[subQ2,-1.0]])],"derivedFrom":subQ1}),1.0]])]});}
            var Q71;
            {var subQ0=sQuery(id+"F0.wireOp",EDGE,"E7.bottom");var subQ1=sQuery(id+"F0.wireOp",EDGE,"E2.left");var subQ2=makeQuery(id+"F0.imprint","INTERSECT",VERTEX,{"derivedFrom":[subQ1,subQ0]});Q71=makeQuery(id+"F0.imprint","IMPRINT",FACE,{"disambiguationData":[TD([[makeQuery(id+"F0.imprint","IMPRINT",EDGE,{"disambiguationData":[TD([[subQ2,-1.0]])],"derivedFrom":subQ1}),-1.0]])]});}
            var Q72;
            {var subQ0=sQuery(id+"F0.wireOp",EDGE,"E7.bottom");var subQ1=sQuery(id+"F0.wireOp",EDGE,"E5.left");var subQ2=makeQuery(id+"F0.imprint","INTERSECT",VERTEX,{"derivedFrom":[subQ1,subQ0]});Q72=makeQuery(id+"F0.imprint","IMPRINT",FACE,{"disambiguationData":[TD([[makeQuery(id+"F0.imprint","IMPRINT",EDGE,{"disambiguationData":[TD([[subQ2,-1.0]])],"derivedFrom":subQ1}),-1.0]])]});}
            var Q73;
            {var subQ5=sQuery(id+"F0.wireOp",EDGE,"E7.left");Q73=makeQuery(id+"F0.imprint","IMPRINT",FACE,{"disambiguationData":[TD([[makeQuery(id+"F0.imprint","IMPRINT",EDGE,{"derivedFrom":subQ5}),1.0]])]});}
            var Q74;
            {var subQ5=sQuery(id+"F0.wireOp",EDGE,"E8.left");Q74=makeQuery(id+"F0.imprint","IMPRINT",FACE,{"disambiguationData":[TD([[makeQuery(id+"F0.imprint","IMPRINT",EDGE,{"derivedFrom":subQ5}),1.0]])]});}
            var Q75;
            {var subQ0=sQuery(id+"F0.wireOp",EDGE,"E8.bottom");var subQ1=sQuery(id+"F0.wireOp",EDGE,"E5.left");var subQ2=makeQuery(id+"F0.imprint","INTERSECT",VERTEX,{"derivedFrom":[subQ1,subQ0]});Q75=makeQuery(id+"F0.imprint","IMPRINT",FACE,{"disambiguationData":[TD([[makeQuery(id+"F0.imprint","IMPRINT",EDGE,{"disambiguationData":[TD([[subQ2,-1.0]])],"derivedFrom":subQ1}),-1.0]])]});}
            var Q76;
            {var subQ0=sQuery(id+"F0.wireOp",EDGE,"E8.bottom");var subQ1=sQuery(id+"F0.wireOp",EDGE,"E2.left");var subQ2=makeQuery(id+"F0.imprint","INTERSECT",VERTEX,{"derivedFrom":[subQ1,subQ0]});Q76=makeQuery(id+"F0.imprint","IMPRINT",FACE,{"disambiguationData":[TD([[makeQuery(id+"F0.imprint","IMPRINT",EDGE,{"disambiguationData":[TD([[subQ2,-1.0]])],"derivedFrom":subQ1}),-1.0]])]});}
            var Q77;
            {var subQ0=sQuery(id+"F0.wireOp",EDGE,"E8.bottom");var subQ1=sQuery(id+"F0.wireOp",EDGE,"E2.right");var subQ2=makeQuery(id+"F0.imprint","INTERSECT",VERTEX,{"derivedFrom":[subQ1,subQ0]});Q77=makeQuery(id+"F0.imprint","IMPRINT",FACE,{"disambiguationData":[TD([[makeQuery(id+"F0.imprint","IMPRINT",EDGE,{"disambiguationData":[TD([[subQ2,-1.0]])],"derivedFrom":subQ1}),1.0]])]});}
            var Q78;
            {var subQ0=sQuery(id+"F0.wireOp",EDGE,"E8.bottom");var subQ1=sQuery(id+"F0.wireOp",EDGE,"E3.right");var subQ2=makeQuery(id+"F0.imprint","INTERSECT",VERTEX,{"derivedFrom":[subQ1,subQ0]});Q78=makeQuery(id+"F0.imprint","IMPRINT",FACE,{"disambiguationData":[TD([[makeQuery(id+"F0.imprint","IMPRINT",EDGE,{"disambiguationData":[TD([[subQ2,-1.0]])],"derivedFrom":subQ1}),1.0]])]});}
            var Q79;
            {var subQ5=sQuery(id+"F0.wireOp",EDGE,"E8.right");Q79=makeQuery(id+"F0.imprint","IMPRINT",FACE,{"disambiguationData":[TD([[makeQuery(id+"F0.imprint","IMPRINT",EDGE,{"derivedFrom":subQ5}),-1.0]])]});}
            var Q80;
            {var subQ5=sQuery(id+"F0.wireOp",EDGE,"E9.right");Q80=makeQuery(id+"F0.imprint","IMPRINT",FACE,{"disambiguationData":[TD([[makeQuery(id+"F0.imprint","IMPRINT",EDGE,{"derivedFrom":subQ5}),1.0]])]});}
            var Q81;
            {var subQ0=sQuery(id+"F0.wireOp",EDGE,"E9.top");var subQ1=sQuery(id+"F0.wireOp",EDGE,"E3.right");var subQ2=makeQuery(id+"F0.imprint","INTERSECT",VERTEX,{"derivedFrom":[subQ1,subQ0]});Q81=makeQuery(id+"F0.imprint","IMPRINT",FACE,{"disambiguationData":[TD([[makeQuery(id+"F0.imprint","IMPRINT",EDGE,{"disambiguationData":[TD([[subQ2,-1.0]])],"derivedFrom":subQ1}),1.0]])]});}
            var Q82;
            {var subQ0=sQuery(id+"F0.wireOp",EDGE,"E9.top");var subQ1=sQuery(id+"F0.wireOp",EDGE,"E2.right");var subQ2=makeQuery(id+"F0.imprint","INTERSECT",VERTEX,{"derivedFrom":[subQ1,subQ0]});Q82=makeQuery(id+"F0.imprint","IMPRINT",FACE,{"disambiguationData":[TD([[makeQuery(id+"F0.imprint","IMPRINT",EDGE,{"disambiguationData":[TD([[subQ2,-1.0]])],"derivedFrom":subQ1}),1.0]])]});}
            var Q83;
            {var subQ0=sQuery(id+"F0.wireOp",EDGE,"E9.top");var subQ1=sQuery(id+"F0.wireOp",EDGE,"E2.left");var subQ2=makeQuery(id+"F0.imprint","INTERSECT",VERTEX,{"derivedFrom":[subQ1,subQ0]});Q83=makeQuery(id+"F0.imprint","IMPRINT",FACE,{"disambiguationData":[TD([[makeQuery(id+"F0.imprint","IMPRINT",EDGE,{"disambiguationData":[TD([[subQ2,-1.0]])],"derivedFrom":subQ1}),-1.0]])]});}
            var Q84;
            {var subQ0=sQuery(id+"F0.wireOp",EDGE,"E9.top");var subQ1=sQuery(id+"F0.wireOp",EDGE,"E5.left");var subQ2=makeQuery(id+"F0.imprint","INTERSECT",VERTEX,{"derivedFrom":[subQ1,subQ0]});Q84=makeQuery(id+"F0.imprint","IMPRINT",FACE,{"disambiguationData":[TD([[makeQuery(id+"F0.imprint","IMPRINT",EDGE,{"disambiguationData":[TD([[subQ2,-1.0]])],"derivedFrom":subQ1}),-1.0]])]});}
            var Q85;
            {var subQ5=sQuery(id+"F0.wireOp",EDGE,"E9.left");Q85=makeQuery(id+"F0.imprint","IMPRINT",FACE,{"disambiguationData":[TD([[makeQuery(id+"F0.imprint","IMPRINT",EDGE,{"derivedFrom":subQ5}),-1.0]])]});}
            extrude(context, id + "F1", {"entities" : qUnion([Q0, Q1, Q2, Q3, Q4, Q5, Q6, Q7, Q8, Q9, Q10, Q11, Q12, Q13, Q14, Q15, Q16, Q17, Q18, Q19, Q20, Q21, Q22, Q23, Q24, Q25, Q26, Q27, Q28, Q29, Q30, Q31, Q32, Q33, Q34, Q35, Q36, Q37, Q38, Q39, Q40, Q41, Q42, Q43, Q44, Q45, Q46, Q47, Q48, Q49, Q50, Q51, Q52, Q53, Q54, Q55, Q56, Q57, Q58, Q59, Q60, Q61, Q62, Q63, Q64, Q65, Q66, Q67, Q68, Q69, Q70, Q71, Q72, Q73, Q74, Q75, Q76, Q77, Q78, Q79, Q80, Q81, Q82, Q83, Q84, Q85]), "depth" : 3.05 * mm});
        }
        {
            var Q0;
            Q0=makeQuery(id+"F1.opExtrude","CAP_EDGE",EDGE,{"disambiguationData":[OSD([sQuery(id+"F0.wireOp",EDGE,"E0.left")])],"isStart":false});
            var Q1;
            Q1=makeQuery(id+"F1.opExtrude","CAP_EDGE",EDGE,{"disambiguationData":[OSD([sQuery(id+"F0.wireOp",EDGE,"E0.top")])],"isStart":false});
            var Q2;
            Q2=makeQuery(id+"F1.opExtrude","CAP_EDGE",EDGE,{"disambiguationData":[OSD([sQuery(id+"F0.wireOp",EDGE,"E0.right")])],"isStart":false});
            var Q3;
            Q3=makeQuery(id+"F1.opExtrude","CAP_EDGE",EDGE,{"disambiguationData":[OSD([sQuery(id+"F0.wireOp",EDGE,"E0.bottom")])],"isStart":false});
            chamfer(context, id + "F2", {"entities" : qUnion([Q0, Q1, Q2, Q3]), "width" : 1.27 * mm, "tangentPropagation" : true});
        }
    });
